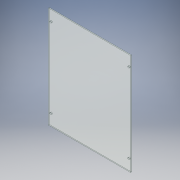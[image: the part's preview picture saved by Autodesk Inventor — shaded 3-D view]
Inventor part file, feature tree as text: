
AUTODESK INVENTOR PART (.ipt)
format: ipt  version: 2019 (Build 230136000, 136)  size: 113,152 bytes
history: native  units: mm
features: extrude x2, sketch x2
ambient origin geometry x8: Origin, YZ Plane, XZ Plane, XY Plane, X Axis, Y Axis, Z Axis, Center Point
bodies: Solid1 (feature_tree)
feature tree (4):
  extrude  "Extrusion1"  Depth=460.0mm
  extrude  "Extrusion2"  Depth=4.0mm
  sketch  "Sketch1"  dims[d0=373.0mm d1=460.0mm]
  sketch  "Sketch2"  dims[d2=4.0mm d3=0.0mm d4=8.0mm d5=8.0mm d6=8.0mm d7=8.0mm d8=50.0mm d9=9.5mm d10=50.0mm d11=9.5mm d12=50.0mm d13=9.5mm d14=50.0mm d15=9.5mm d16=4.0mm d17=0.0mm]
